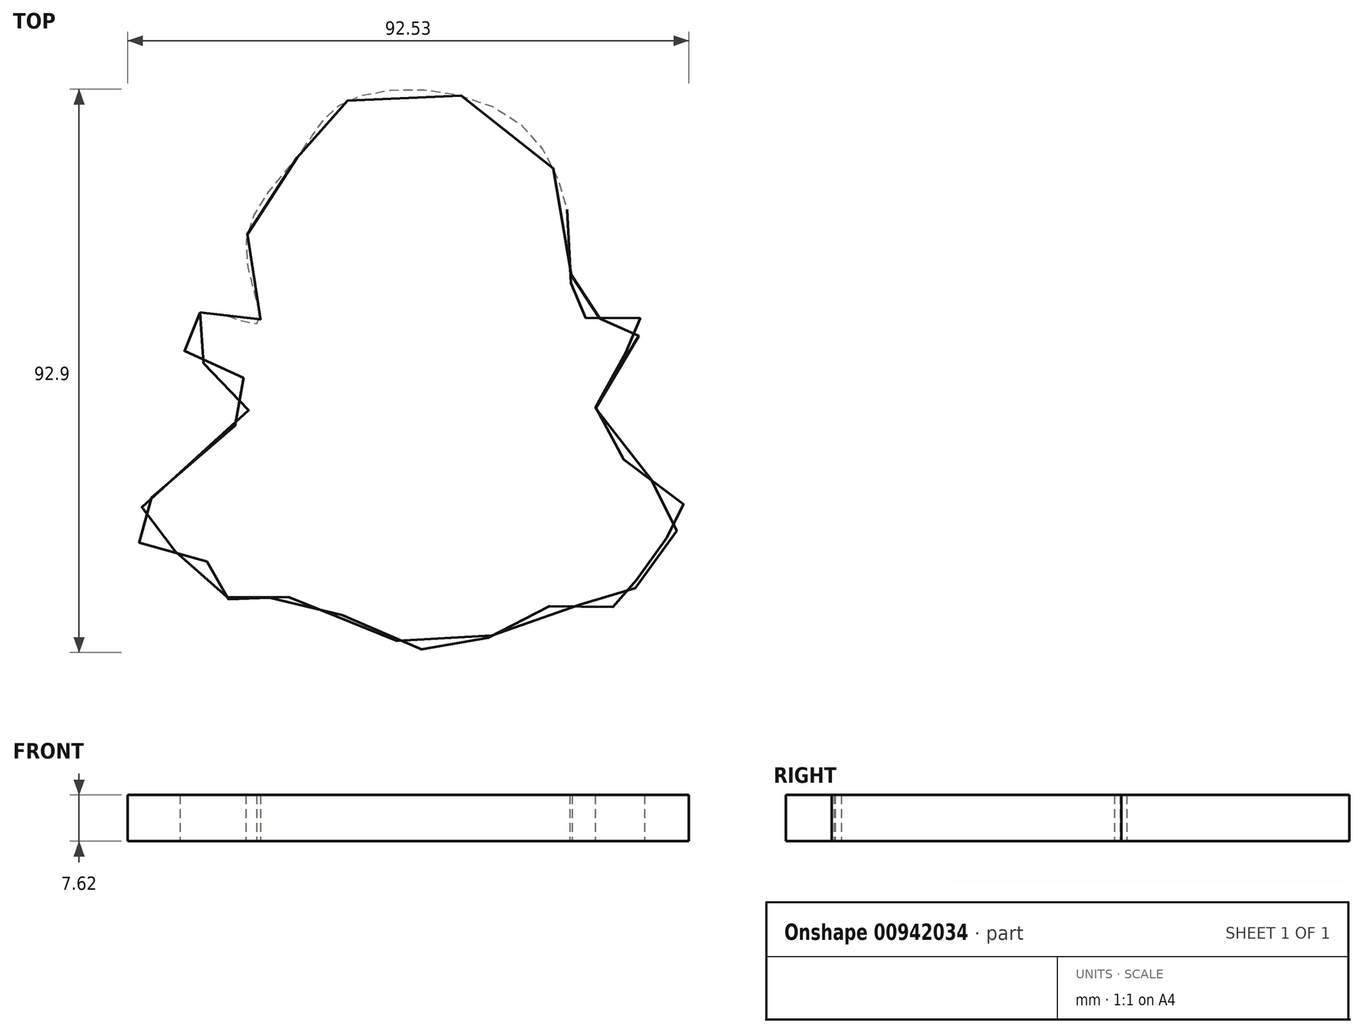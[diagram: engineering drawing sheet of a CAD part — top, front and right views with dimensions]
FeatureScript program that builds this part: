
annotation { "Feature Type Name" : "Feature", "Feature Type Description" : "" }
export const myFeature = defineFeature(function(context is Context, id is Id, definition is map)
    precondition{}
    {
        {
            var Q0;
            Q0=qCreatedBy(makeId("Top.planeOp"),FACE);
            var sketch = newSketch(context, id + "F0", { "sketchPlane" : qUnion([Q0])});
            skFitSpline(sketch, "E0", {"points": [v(-36.35, 13.29) * mm, v(-26.72, 11.53) * mm, v(-28.76, 24.38) * mm, v(-20, 39.27) * mm, v(-11.83, 48.33) * mm, v(15.91, 44.82) * mm, v(24.97, 20.88) * mm, v(26.13, 12.7) * mm, v(36.65, 12.12) * mm, v(31.97, 4.23) * mm, v(30.22, -7.74) * mm, v(44.24, -20) * mm, v(36.94, -27.01) * mm, v(34.31, -34.6) * mm, v(21.17, -35.19) * mm, v(3.94, -42.78) * mm, v(-21.46, -33.73) * mm, v(-31.4, -34.31) * mm, v(-34.6, -28.18) * mm, v(-48.29, -22.67) * mm, v(-27.02, 0) * mm, v(-38.84, 6.87) * mm, v(-36.35, 13.29) * mm]});
            skSolve(sketch);
        }
        {
            var Q0;
            Q0=makeQuery(id+"F0.imprint","IMPRINT",FACE,{"disambiguationData":[TD([[makeQuery(id+"F0.imprint","IMPRINT",EDGE,{"derivedFrom":sQuery(id+"F0.wireOp",EDGE,"E0")}),-1.0]])]});
            extrude(context, id + "F1", {"entities" : qUnion([Q0]), "depth" : 7.62 * mm, "offsetDistance" : 25.4 * mm});
        }
    });
